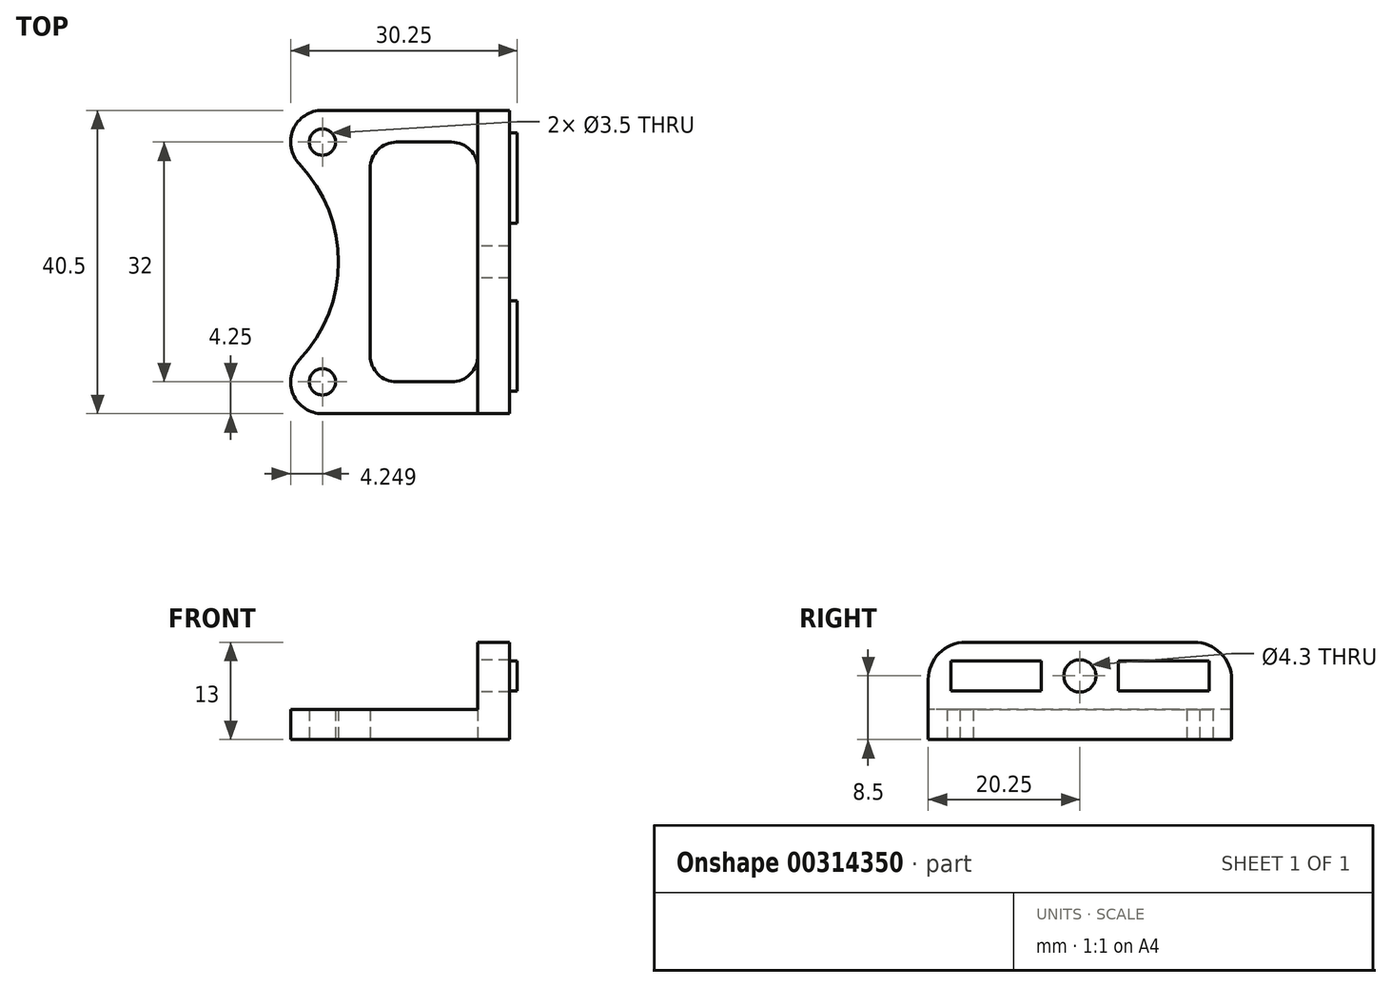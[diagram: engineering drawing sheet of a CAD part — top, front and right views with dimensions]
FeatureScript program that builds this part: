
annotation { "Feature Type Name" : "Feature", "Feature Type Description" : "" }
export const myFeature = defineFeature(function(context is Context, id is Id, definition is map)
    precondition{}
    {
        {
            var Q0;
            Q0=qCreatedBy(makeId("Top.planeOp"),FACE);
            var sketch = newSketch(context, id + "F0", { "sketchPlane" : qUnion([Q0])});
            skCircle(sketch, "E0", {"center": v(-6.38, 16) * mm, "radius": 1.75 * mm});
            skCircle(sketch, "E1", {"center": v(-6.38, -16) * mm, "radius": 1.75 * mm});
            skLineSegment(sketch, "E2", {"start": v(-6.38, -16) * mm, "end": v(-6.38, 16) * mm, "construction": true});
            skArc(sketch, "E3.0", {"start": v(-6.38, 20.25) * mm, "mid": v(-10.29, 17.68) * mm, "end": v(-9.46, 13.08) * mm});
            skArc(sketch, "E4.0", {"start": v(-9.46, -13.08) * mm, "mid": v(-10.29, -17.68) * mm, "end": v(-6.38, -20.25) * mm});
            skArc(sketch, "E5", {"start": v(-9.46, -13.08) * mm, "mid": v(-4.25, 0) * mm, "end": v(-9.46, 13.08) * mm});
            skLineSegment(sketch, "E6", {"start": v(18.62, 20.25) * mm, "end": v(-6.38, 20.25) * mm});
            skLineSegment(sketch, "E7", {"start": v(-4.25, 0) * mm, "end": v(0, 0) * mm, "construction": true});
            skLineSegment(sketch, "E8", {"start": v(18.62, 20.25) * mm, "end": v(18.62, 0) * mm});
            skLineSegment(sketch, "E9.MirrorCS", {"start": v(18.62, -20.25) * mm, "end": v(-6.38, -20.25) * mm});
            skLineSegment(sketch, "E10.MirrorCS", {"start": v(18.62, -20.25) * mm, "end": v(18.62, 0) * mm});
            skLineSegment(sketch, "E11.bottom", {"start": v(10.87, 16) * mm, "end": v(3.5, 16) * mm});
            skLineSegment(sketch, "E11.top", {"start": v(10.87, -16) * mm, "end": v(3.5, -16) * mm});
            skLineSegment(sketch, "E11.left", {"start": v(14.37, 12.5) * mm, "end": v(14.37, -12.5) * mm});
            skLineSegment(sketch, "E11.right", {"start": v(0, 12.5) * mm, "end": v(0, -12.5) * mm});
            skLineSegment(sketch, "E12", {"start": v(6.1, 20.25) * mm, "end": v(6.1, 16) * mm, "construction": true});
            skLineSegment(sketch, "E13", {"start": v(18.62, 0) * mm, "end": v(14.37, 0) * mm, "construction": true});
            skLineSegment(sketch, "E14", {"start": v(5.12, -16) * mm, "end": v(5.12, -20.25) * mm, "construction": true});
            skPoint(sketch, "E15.visualSharp", {"position": v(0, 16) * mm});
            skArc(sketch, "E15.filletArc", {"start": v(3.5, 16) * mm, "mid": v(1.03, 14.97) * mm, "end": v(0, 12.5) * mm});
            skPoint(sketch, "E16.visualSharp", {"position": v(14.37, 16) * mm});
            skArc(sketch, "E16.filletArc", {"start": v(14.37, 12.5) * mm, "mid": v(13.34, 14.97) * mm, "end": v(10.87, 16) * mm});
            skPoint(sketch, "E17.visualSharp", {"position": v(14.37, -16) * mm});
            skArc(sketch, "E17.filletArc", {"start": v(10.87, -16) * mm, "mid": v(13.34, -14.97) * mm, "end": v(14.37, -12.5) * mm});
            skPoint(sketch, "E18.visualSharp", {"position": v(0, -16) * mm});
            skArc(sketch, "E18.filletArc", {"start": v(0, -12.5) * mm, "mid": v(1.03, -14.97) * mm, "end": v(3.5, -16) * mm});
            skSolve(sketch);
        }
        {
            var Q0;
            Q0 = qSketchRegion(id + "F0", true);
            extrude(context, id + "F1", {"entities" : qUnion([Q0]), "depth" : 4 * mm});
        }
        {
            var Q0;
            Q0=makeQuery(id+"F1.opExtrude","CAP_FACE",FACE,{"disambiguationData":[OSD([sQuery(id+"F0.wireOp",EDGE,"E0"),sQuery(id+"F0.wireOp",EDGE,"E1"),sQuery(id+"F0.wireOp",EDGE,"E3.0"),sQuery(id+"F0.wireOp",EDGE,"E4.0"),sQuery(id+"F0.wireOp",EDGE,"E5"),sQuery(id+"F0.wireOp",EDGE,"E6"),sQuery(id+"F0.wireOp",EDGE,"E8"),sQuery(id+"F0.wireOp",EDGE,"E9.MirrorCS"),sQuery(id+"F0.wireOp",EDGE,"E10.MirrorCS"),sQuery(id+"F0.wireOp",EDGE,"E11.bottom"),sQuery(id+"F0.wireOp",EDGE,"E11.top"),sQuery(id+"F0.wireOp",EDGE,"E11.left"),sQuery(id+"F0.wireOp",EDGE,"E11.right"),sQuery(id+"F0.wireOp",EDGE,"E15.filletArc"),sQuery(id+"F0.wireOp",EDGE,"E16.filletArc"),sQuery(id+"F0.wireOp",EDGE,"E17.filletArc"),sQuery(id+"F0.wireOp",EDGE,"E18.filletArc")])],"isStart":false});
            var sketch = newSketch(context, id + "F2", { "sketchPlane" : qUnion([Q0])});
            skLineSegment(sketch, "E19.bottom", {"start": v(18.62, 20.25) * mm, "end": v(14.37, 20.25) * mm});
            skLineSegment(sketch, "E19.top", {"start": v(18.62, -20.25) * mm, "end": v(14.37, -20.25) * mm});
            skLineSegment(sketch, "E19.left", {"start": v(18.62, 20.25) * mm, "end": v(18.62, -20.25) * mm});
            skLineSegment(sketch, "E19.right", {"start": v(14.37, 20.25) * mm, "end": v(14.37, -20.25) * mm});
            skSolve(sketch);
        }
        {
            var Q0;
            Q0 = qSketchRegion(id + "F2", true);
            extrude(context, id + "F3", {"entities" : qUnion([Q0]), "operationType" : NewBodyOperationType.ADD, "depth" : 9 * mm});
        }
        {
            var Q0;
            Q0=makeQuery(id+"F3.boolean.opBoolean","MERGE",FACE,{"derivedFrom":[makeQuery(id+"F1.opExtrude","SWEPT_FACE",FACE,{"disambiguationData":[OSD([sQuery(id+"F0.wireOp",EDGE,"E11.left")])]}),makeQuery(id+"F3.opExtrude","SWEPT_FACE",FACE,{"disambiguationData":[OSD([sQuery(id+"F2.wireOp",EDGE,"E19.right")])]})]});
            var sketch = newSketch(context, id + "F4", { "sketchPlane" : qUnion([Q0])});
            skCircle(sketch, "E20", {"center": v(0, 8.5) * mm, "radius": 2.15 * mm});
            skLineSegment(sketch, "E21", {"start": v(0, 8.5) * mm, "end": v(0, 13) * mm, "construction": true});
            skLineSegment(sketch, "E22", {"start": v(0, 8.5) * mm, "end": v(20.25, 8.5) * mm, "construction": true});
            skSolve(sketch);
        }
        {
            var Q0;
            Q0 = qSketchRegion(id + "F4", true);
            extrude(context, id + "F5", {"entities" : qUnion([Q0]), "operationType" : NewBodyOperationType.REMOVE, "oppositeDirection" : true, "depth" : 25 * mm});
        }
        {
            var Q0;
            Q0=makeQuery(id+"F3.opExtrude","CAP_EDGE",EDGE,{"disambiguationData":[OSD([sQuery(id+"F2.wireOp",EDGE,"E19.top")])],"isStart":false});
            var Q1;
            Q1=makeQuery(id+"F3.opExtrude","CAP_EDGE",EDGE,{"disambiguationData":[OSD([sQuery(id+"F2.wireOp",EDGE,"E19.bottom")])],"isStart":false});
            fillet(context, id + "F6", {"entities" : qUnion([Q0, Q1]), "radius" : 5 * mm, "tangentPropagation" : true, "allowEdgeOverflow" : false});
        }
        {
            var Q0;
            Q0=makeQuery(id+"F3.boolean.opBoolean","MERGE",FACE,{"derivedFrom":[makeQuery(id+"F1.opExtrude","SWEPT_FACE",FACE,{"disambiguationData":[OSD([sQuery(id+"F0.wireOp",EDGE,"E8"),sQuery(id+"F0.wireOp",EDGE,"E10.MirrorCS")])]}),makeQuery(id+"F3.opExtrude","SWEPT_FACE",FACE,{"disambiguationData":[OSD([sQuery(id+"F2.wireOp",EDGE,"E19.left")])]})]});
            var sketch = newSketch(context, id + "F7", { "sketchPlane" : qUnion([Q0])});
            skLineSegment(sketch, "E23.bottom", {"start": v(-17.25, 10.5) * mm, "end": v(-5.15, 10.5) * mm});
            skLineSegment(sketch, "E23.top", {"start": v(-17.25, 6.5) * mm, "end": v(-5.15, 6.5) * mm});
            skLineSegment(sketch, "E23.left", {"start": v(-17.25, 10.5) * mm, "end": v(-17.25, 6.5) * mm});
            skLineSegment(sketch, "E23.right", {"start": v(-5.15, 10.5) * mm, "end": v(-5.15, 6.5) * mm});
            skLineSegment(sketch, "E24", {"start": v(0, 13) * mm, "end": v(0, 0) * mm, "construction": true});
            skLineSegment(sketch, "E25", {"start": v(0, 8.5) * mm, "end": v(-17.25, 8.5) * mm, "construction": true});
            skLineSegment(sketch, "E26.MirrorCS", {"start": v(17.25, 6.5) * mm, "end": v(5.15, 6.5) * mm});
            skLineSegment(sketch, "E27.MirrorCS", {"start": v(5.15, 10.5) * mm, "end": v(5.15, 6.5) * mm});
            skLineSegment(sketch, "E28.MirrorCS", {"start": v(17.25, 10.5) * mm, "end": v(5.15, 10.5) * mm});
            skLineSegment(sketch, "E29.MirrorCS", {"start": v(17.25, 10.5) * mm, "end": v(17.25, 6.5) * mm});
            skSolve(sketch);
        }
        {
            var Q0;
            Q0 = qSketchRegion(id + "F7", true);
            extrude(context, id + "F8", {"entities" : qUnion([Q0]), "operationType" : NewBodyOperationType.ADD, "depth" : 1 * mm});
        }
    });
